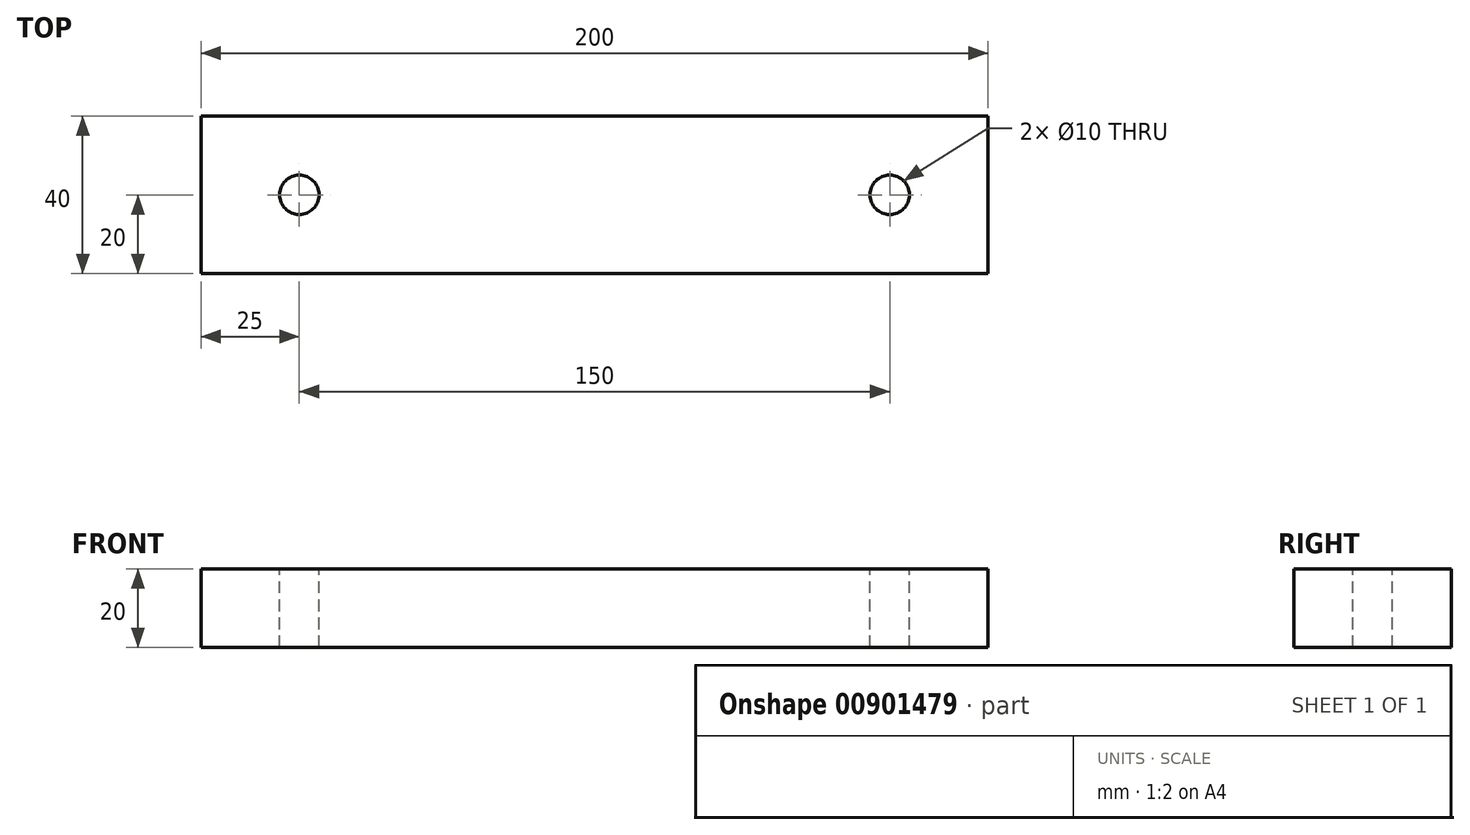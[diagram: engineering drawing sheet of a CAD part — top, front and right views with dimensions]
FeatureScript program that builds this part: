
annotation { "Feature Type Name" : "Feature", "Feature Type Description" : "" }
export const myFeature = defineFeature(function(context is Context, id is Id, definition is map)
    precondition{}
    {
        {
            var Q0;
            Q0=qCreatedBy(makeId("Top.planeOp"),FACE);
            var sketch = newSketch(context, id + "F0", { "sketchPlane" : qUnion([Q0])});
            skLineSegment(sketch, "E0.bottom", {"start": v(100, 20) * mm, "end": v(-100, 20) * mm});
            skLineSegment(sketch, "E0.top", {"start": v(100, -20) * mm, "end": v(-100, -20) * mm});
            skLineSegment(sketch, "E0.left", {"start": v(100, 20) * mm, "end": v(100, -20) * mm});
            skLineSegment(sketch, "E0.right", {"start": v(-100, 20) * mm, "end": v(-100, -20) * mm});
            skPoint(sketch, "E0.middle", {"position": v(0, 0) * mm});
            skSolve(sketch);
        }
        {
            var Q0;
            Q0 = qSketchRegion(id + "F0", true);
            extrude(context, id + "F1", {"entities" : qUnion([Q0]), "depth" : 20 * mm, "offsetDistance" : 25 * mm});
        }
        {
            var Q0;
            Q0=makeQuery(id+"F1.opExtrude","CAP_FACE",FACE,{"disambiguationData":[OSD([sQuery(id+"F0.wireOp",EDGE,"E0.bottom"),sQuery(id+"F0.wireOp",EDGE,"E0.top"),sQuery(id+"F0.wireOp",EDGE,"E0.left"),sQuery(id+"F0.wireOp",EDGE,"E0.right")])],"isStart":false});
            var sketch = newSketch(context, id + "F2", { "sketchPlane" : qUnion([Q0])});
            skCircle(sketch, "E1", {"center": v(75, 0) * mm, "radius": 5 * mm});
            skCircle(sketch, "E2", {"center": v(-75, 0) * mm, "radius": 5 * mm});
            skLineSegment(sketch, "E3", {"start": v(0, -10.68) * mm, "end": v(0, 15.67) * mm, "construction": true});
            skSolve(sketch);
        }
        {
            var Q0;
            Q0 = qSketchRegion(id + "F2", true);
            extrude(context, id + "F3", {"entities" : qUnion([Q0]), "operationType" : NewBodyOperationType.REMOVE, "endBound" : BoundingType.THROUGH_ALL, "oppositeDirection" : true, "depth" : 25 * mm, "offsetDistance" : 25 * mm});
        }
    });
